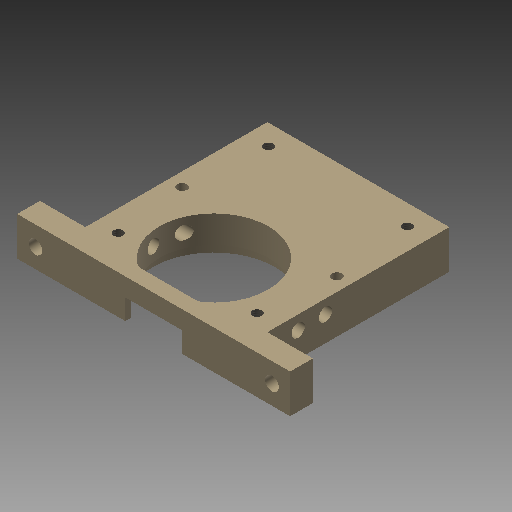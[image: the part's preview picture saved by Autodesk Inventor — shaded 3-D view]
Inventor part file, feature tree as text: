
AUTODESK INVENTOR PART (.ipt)
format: ipt  version: 2018 (Build 220112000, 112)  size: 340,480 bytes
history: native  units: mm
features: extrude x11, sketch x6, projected_geometry x5, hole x4, mirror x3, reference x2, chamfer x1, fillet x1, other x1
ambient origin geometry x8: Origin, YZ Plane, XZ Plane, XY Plane, X Axis, Y Axis, Z Axis, Center Point
bodies: Volumenkörper1 (feature_tree)
feature tree (34):
  extrude  "Extrusion1"  Depth=90.0mm
  extrude  "Extrusion2"  Depth=25.0mm
  extrude  "Extrusion3"  Depth=8.0mm
  extrude  "Extrusion4"  Depth=8.0mm
  mirror  "Spiegeln1"
  chamfer  "Fase1"  Distance=4.1mm
  hole  "Bohrung3"  [1 undecoded]
  sketch  "Skizze11"  dims[d5=12.0mm d6=0.0mm d14=8.0mm]
  sketch  "Skizze12"  dims[d15=8.0mm d16=8.0mm]
  extrude  "Extrusion8"  Depth=10.0mm
  extrude  "Extrusion9"  Depth=10.0mm
  extrude  "Extrusion10"  Depth=10.0mm
  extrude  "Extrusion11"  Depth=10.0mm
  fillet  "Rundung1"  Radius=1.5mm
  extrude  "Extrusion13"  Depth=10.0mm TaperAngle=0.0deg
  extrude  "Extrusion14"  Depth=10.0mm TaperAngle=45.0deg
  hole  "Bohrung4"  [1 undecoded]
  extrude  "Extrusion17"  Depth=10.0mm
  hole  "Bohrung5"  [1 undecoded]
  mirror  "Spiegeln2"
  other  "Fläche verschieben3"
  hole  "Bohrung6"  [1 undecoded]
  mirror  "Spiegeln3"
  reference  "Referenz1"
  sketch  "Skizze6"  dims[d0=80.0mm d1=90.0mm]
  sketch  "Skizze8"  dims[d2=12.0mm d3=0.0mm d4=25.0mm]
  projected_geometry  "Projizierte Kontur2"
  projected_geometry  "Projizierte Kontur3"
  projected_geometry  "Projizierte Kontur4"
  sketch  "Skizze14"  dims[d17=8.0mm d18=4.1mm d19=0.0mm]
  projected_geometry  "Projizierte Kontur5"
  projected_geometry  "Projizierte Kontur6"
  sketch  "Skizze21"  dims[d22=33.0mm d23=39.0mm d24=7.5mm d25=19.5mm d27=19.5mm d28=23.5mm d29=1.5mm d31=5.0mm d32=0.0mm d33=2.0mm d34=2.0mm d35=45.0deg d45=12.0mm d46=4.0mm d47=5.9mm d48=6.0mm d49=4.0mm d50=2.0mm d51=90.0deg d52=8.0mm d53=20.594885mm d60=50.0mm d61=54.0mm d64=25.0mm d65=12.5mm d66=5.0mm d67=2.0mm d70=50.0mm d71=7.5mm d72=0.0mm d73=4.0mm d74=0.0mm d75=1.5mm d77=1.0mm d78=10.0mm d79=0.0mm d80=10.0mm d81=0.0mm d82=4.0mm d85=10.0mm d86=0.0mm d87=1.5mm d88=1.2mm d89=5.0mm d90=0.0mm d99=5.0mm d101=64.0mm d112=1.2mm d113=61.0mm d114=66.0mm d115=15.0mm d116=9.5mm d117=4.134mm d118=6.0mm d119=4.0mm d120=2.0mm d121=90.0deg d122=8.0mm d123=20.594885mm d124=20.0mm d125=17.0mm d126=10.0mm d127=0.0mm d128=8.0mm d129=6.0mm d130=6.0mm d131=4.0mm d132=2.0mm d133=90.0deg d134=8.0mm d135=20.594885mm d136=6.0mm d137=46.5mm d138=4.4mm d139=6.0mm d140=4.0mm d141=2.0mm d142=90.0deg d143=8.0mm d144=20.594885mm]
  reference  "Referenz8"
note: 4 required parameter values undecoded (feature->parameter linkage not recoverable at this tier; creation-order binding heuristic only, values carry confidence <= 0.55)
